# Revit family: Domotics-DomesticRanges-GEWISS-SYSTEM_POWER-SOCKET-OUTLET_ITADEU_P30_16A
name_source: partatom
category: Apparecchi elettrici
revit_build: Autodesk Revit 2016 (Build: 20161004_0715(x64)
units: mm (PartAtom-declared; Revit-internal decimal feet)

## family parameters
Condiviso = Sì
Host = Superficie
Mantenere orientamento annotazione = Sì
Numero OmniClass = 23.80.50.14
Punto di calcolo locali = Sì
Quota connettore circolare = Usa diametro
Taglio con vuoti quando caricato = No
Tipo di parte = Normale
Titolo OmniClass = Plug Connectors

## types (2) — shared parameters
Catalogue = DOMOTICS
Catalogue Range = SYSTEM - DOMESTIC RANGE
Description: = 2P+E - 16A
Earth pit = Side and central
Electrocod = 0131
For plug pins = Ã˜ 4 / 4.8 mm
GW - Testo elettrico = UNEL
IDF = c6428bf3-62b9-440f-ad57-68dc78301340
IDT = df81c5e5-2c0c-4c2a-931f-c685a58514bb
Immagine tipo = GW21205.jpg
Larghezza presa = 46 mm  [stored 0.150919 ft]
No. SYSTEM modules = 2
Produttore = GEWISS S.p.A.
Prospetto di default = 1219 mm
SEO = Socket outlet
Simbolo = SIMBOLO PRESE : PRESA
Standard: = Italian / German
Technical sheet = https://www.gewiss.com
Tipo_ = SYSTEM-PRESA-ITA GER-P30-16A_BASE : GW21205 - PRESA 2P+T 16A ST.ITALIANO/TED.SY/BK
Type = P30
URL = https://www.gewiss.com
Version file RFA = 19.4
Voltage: = 250 V ac

## per-type parameters (varying)
| type | Colour | Description. | Descrizione | EAN code | Modello |
| GW20205 - 16A 2P+E ITALIAN/GERMAN S.-OUTLET SY/WT | White | Socket-outlet 16 A | 16A 2P+E ITALIAN/GERMAN S.-OUTLET SY/WT | 8011564000575 | GW20205 |
| GW21205 - 16A 2P+E ITALIAN/GERMAN S.-OUTLET SY/BK | Black | Dual amperage socket-outlet | 16A 2P+E ITALIAN/GERMAN S.-OUTLET SY/BK | 8011564128415 | GW21205 |

note: [stored X ft] marks values corroborated as IEEE doubles in the binary element streams (Revit-internal decimal feet)

## geometry (parser evidence)
native form markers: Sweep x1
no freeform markers — native parametric forms only
